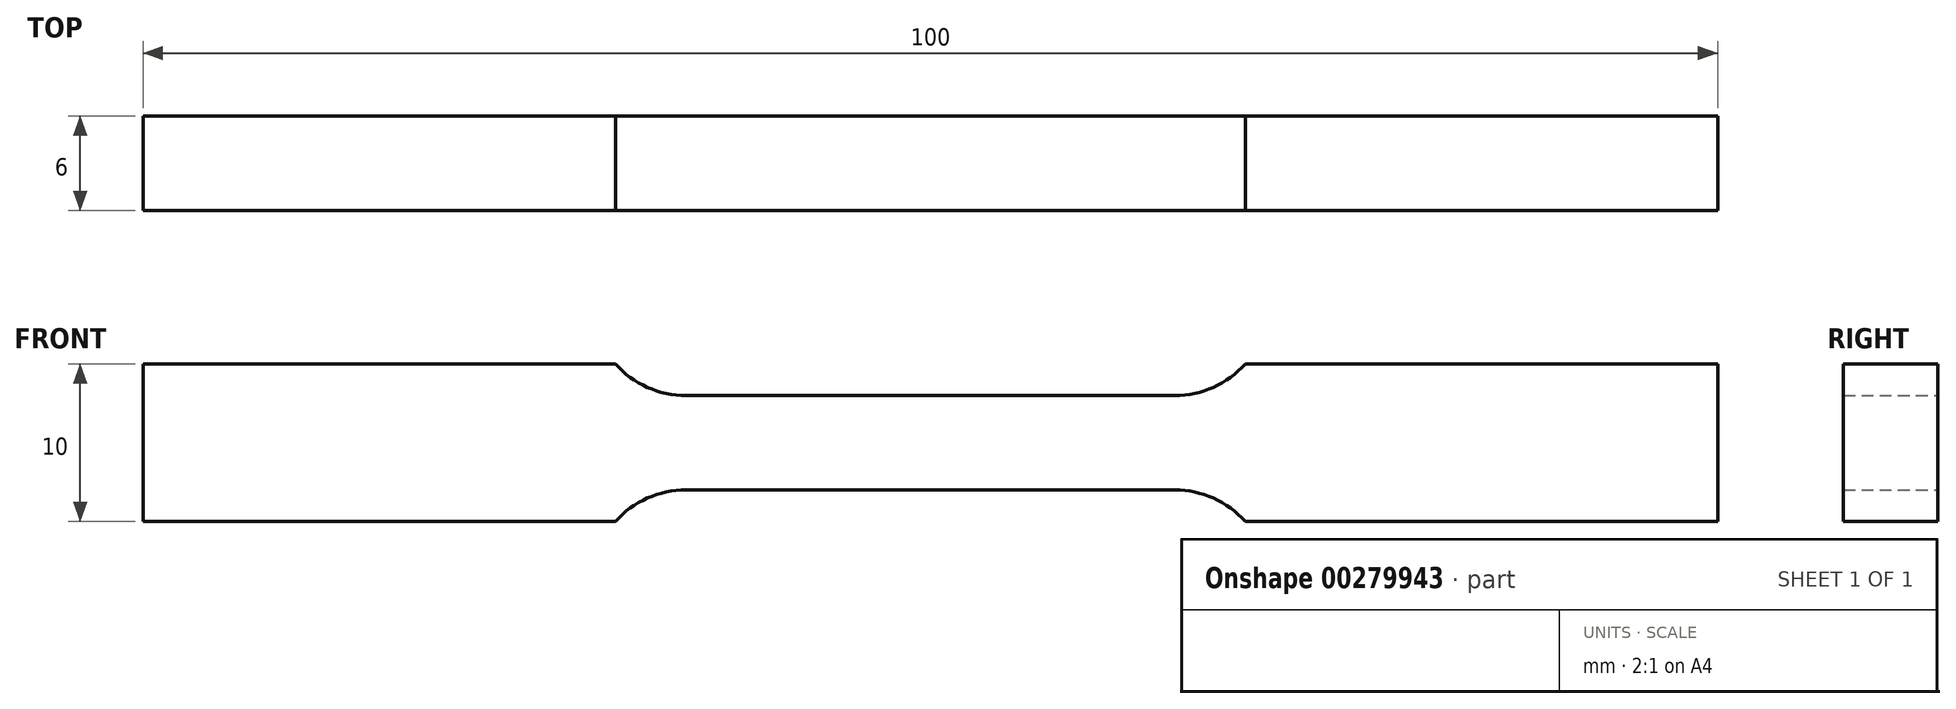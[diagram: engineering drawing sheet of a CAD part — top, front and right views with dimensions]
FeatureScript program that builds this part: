
annotation { "Feature Type Name" : "Feature", "Feature Type Description" : "" }
export const myFeature = defineFeature(function(context is Context, id is Id, definition is map)
    precondition{}
    {
        {
            var Q0;
            Q0=qCreatedBy(makeId("Front.planeOp"),FACE);
            var sketch = newSketch(context, id + "F0", { "sketchPlane" : qUnion([Q0])});
            skLineSegment(sketch, "E0", {"start": v(0, 3) * mm, "end": v(15.53, 3) * mm});
            skArc(sketch, "E1", {"start": v(15.53, 3) * mm, "mid": v(17.98, 3.52) * mm, "end": v(20, 5) * mm});
            skLineSegment(sketch, "E2", {"start": v(20, 5) * mm, "end": v(50, 5) * mm});
            skLineSegment(sketch, "E3", {"start": v(50, 5) * mm, "end": v(50, 0) * mm});
            skLineSegment(sketch, "E4.MirrorCS", {"start": v(0, -3) * mm, "end": v(15.53, -3) * mm});
            skLineSegment(sketch, "E5.MirrorCS", {"start": v(50, -5) * mm, "end": v(50, 0) * mm});
            skLineSegment(sketch, "E6.MirrorCS", {"start": v(20, -5) * mm, "end": v(50, -5) * mm});
            skArc(sketch, "E7.MirrorCS", {"start": v(15.53, -3) * mm, "mid": v(17.98, -3.52) * mm, "end": v(20, -5) * mm});
            skArc(sketch, "E8.MirrorCS", {"start": v(-15.53, -3) * mm, "mid": v(-17.98, -3.52) * mm, "end": v(-20, -5) * mm});
            skArc(sketch, "E9.MirrorCS", {"start": v(-15.53, 3) * mm, "mid": v(-17.98, 3.52) * mm, "end": v(-20, 5) * mm});
            skLineSegment(sketch, "E10.MirrorCS", {"start": v(-20, -5) * mm, "end": v(-50, -5) * mm});
            skLineSegment(sketch, "E11.MirrorCS", {"start": v(-20, 5) * mm, "end": v(-50, 5) * mm});
            skLineSegment(sketch, "E12.MirrorCS", {"start": v(-50, -5) * mm, "end": v(-50, 0) * mm});
            skLineSegment(sketch, "E13.MirrorCS", {"start": v(0, -3) * mm, "end": v(-15.53, -3) * mm});
            skLineSegment(sketch, "E14.MirrorCS", {"start": v(-50, 5) * mm, "end": v(-50, 0) * mm});
            skLineSegment(sketch, "E15.MirrorCS", {"start": v(0, 3) * mm, "end": v(-15.53, 3) * mm});
            skSolve(sketch);
        }
        {
            var Q0;
            Q0=makeQuery(id+"F0.imprint","IMPRINT",FACE,{"disambiguationData":[TD([[makeQuery(id+"F0.imprint","IMPRINT",EDGE,{"derivedFrom":sQuery(id+"F0.wireOp",EDGE,"E0")}),-1.0]])]});
            extrude(context, id + "F1", {"entities" : qUnion([Q0]), "endBound" : BoundingType.SYMMETRIC, "depth" : 6 * mm});
        }
    });
